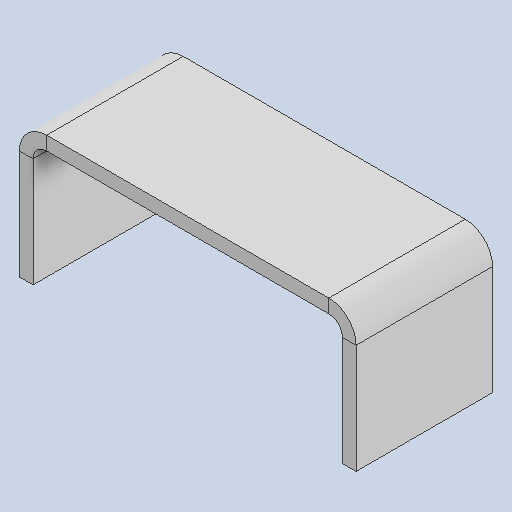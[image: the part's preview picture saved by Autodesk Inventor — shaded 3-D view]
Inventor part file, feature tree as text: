
AUTODESK INVENTOR PART (.ipt)
format: ipt  version: 2025 (Build 290162010, 162A)  size: 114,688 bytes
history: native  units: mm
features: sheet_metal_op x3, sketch x1, other x1
ambient origin geometry x8: Origin, YZ Plane, XZ Plane, XY Plane, X Axis, Y Axis, Z Axis, Center Point
bodies: Solid1 (feature_tree)
feature tree (5):
  sheet_metal_op  "Contour Flange1"
  sketch  "Sketch1"  dims[d0=30.0mm d1=74.0mm d4=3.0mm d5=3.0mm d6=1.5mm d7=6.0mm d8=3.0mm d9=30.0mm d10=3.0mm d11=3.048mm d12=12.0mm d13=3.0mm d14=3.0mm]
  other  "Plate1"
  sheet_metal_op  "Bend1"
  sheet_metal_op  "Corner1"
